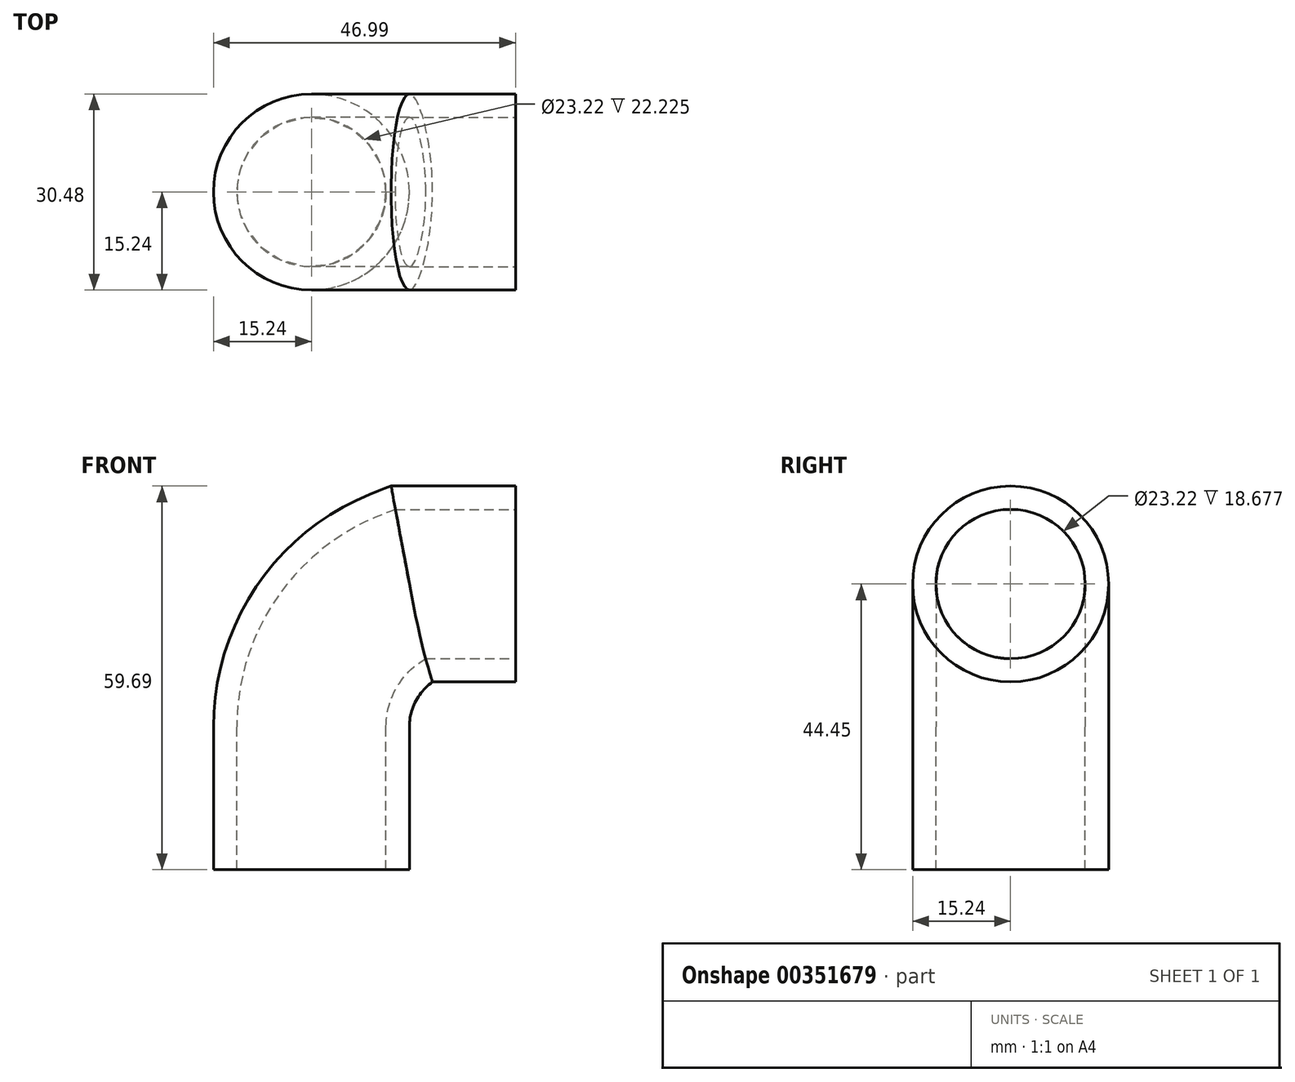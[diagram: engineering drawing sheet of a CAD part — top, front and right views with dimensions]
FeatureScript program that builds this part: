
annotation { "Feature Type Name" : "Feature", "Feature Type Description" : "" }
export const myFeature = defineFeature(function(context is Context, id is Id, definition is map)
    precondition{}
    {
        {
            var Q0;
            Q0=qCreatedBy(makeId("Top.planeOp"),FACE);
            var sketch = newSketch(context, id + "F0", { "sketchPlane" : qUnion([Q0])});
            skCircle(sketch, "E0", {"center": v(0, 0) * mm, "radius": 15.24 * mm});
            skSolve(sketch);
        }
        {
            var Q0;
            Q0=qCreatedBy(makeId("Front.planeOp"),FACE);
            var sketch = newSketch(context, id + "F1", { "sketchPlane" : qUnion([Q0])});
            skLineSegment(sketch, "E1", {"start": v(0, 0) * mm, "end": v(0, 22.23) * mm});
            skArc(sketch, "E2", {"start": v(0, 22.23) * mm, "mid": v(4.18, 35.7) * mm, "end": v(15.24, 44.45) * mm});
            skLineSegment(sketch, "E3", {"start": v(15.24, 44.45) * mm, "end": v(31.75, 44.45) * mm});
            skSolve(sketch);
        }
        {
            var Q0;
            Q0 = qSketchRegion(id + "F0", true);
            var Q1;
            Q1=sQuery(id+"F1.wireOp",EDGE,"E1");
            var Q2;
            Q2=sQuery(id+"F1.wireOp",EDGE,"E2");
            var Q3;
            Q3=sQuery(id+"F1.wireOp",EDGE,"E3");
            sweep(context, id + "F2", {"profiles" : qUnion([Q0]), "path" : qUnion([Q1, Q2, Q3])});
        }
        {
            var Q0;
            Q0=makeQuery(id+"F2.opSweep","CAP_FACE",FACE,{"disambiguationData":[OSD([sQuery(id+"F0.wireOp",EDGE,"E0"),sQuery(id+"F1.wireOp",VERTEX,"E3.end")])],"isStart":false});
            var Q1;
            Q1=makeQuery(id+"F2.opSweep","CAP_FACE",FACE,{"disambiguationData":[OSD([sQuery(id+"F0.wireOp",EDGE,"E0"),sQuery(id+"F1.wireOp",VERTEX,"E1.start")])],"isStart":true});
            shell(context, id + "F3", {"entities" : qUnion([Q0, Q1]), "thickness" : 3.63 * mm});
        }
    });
